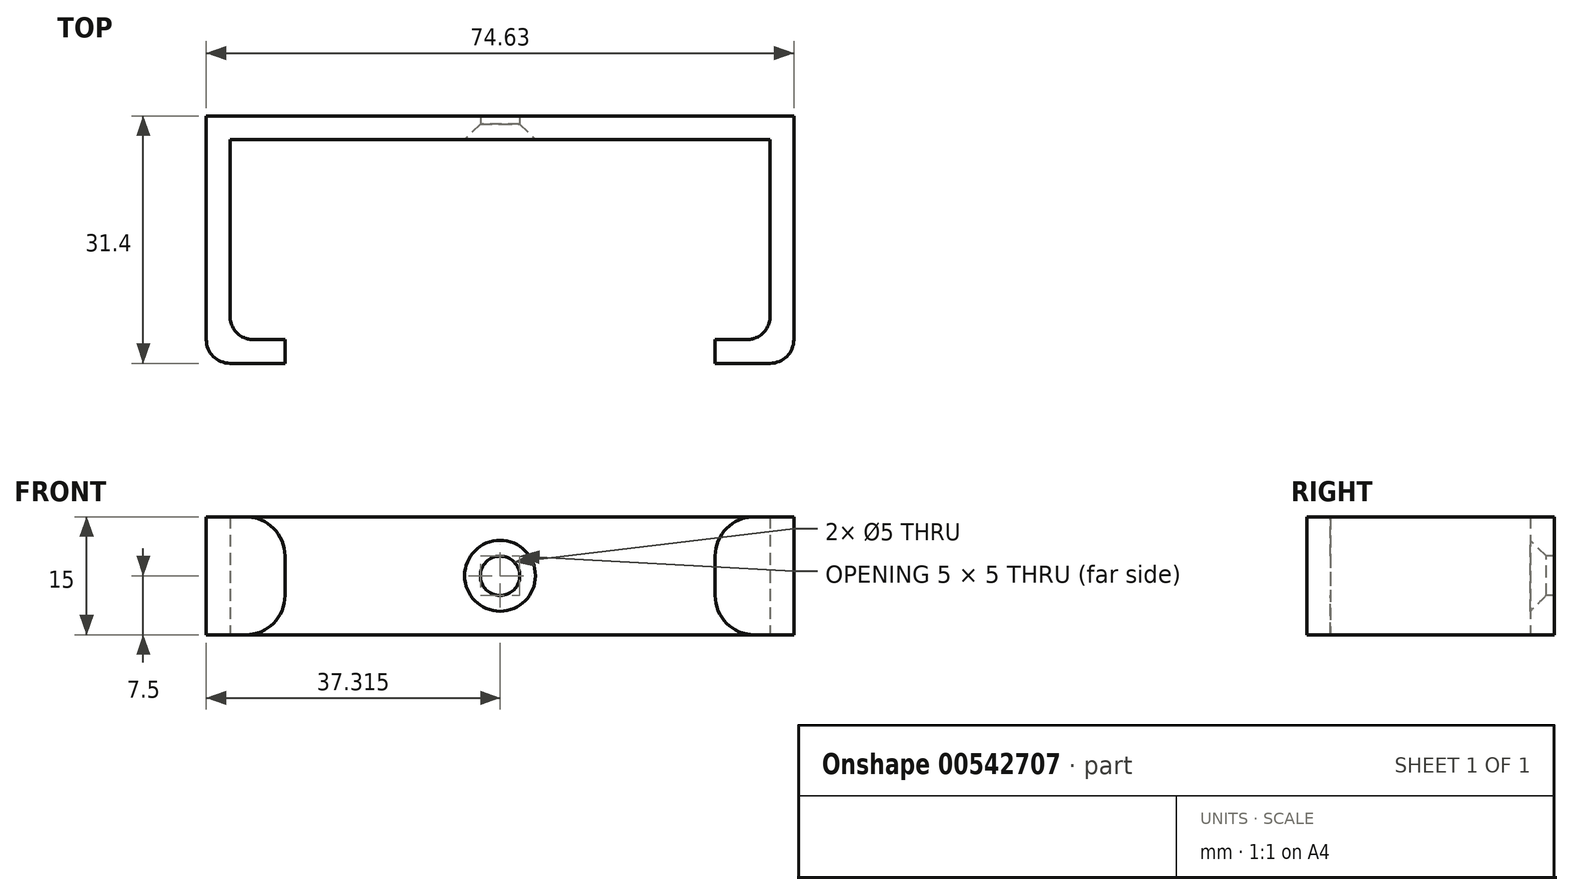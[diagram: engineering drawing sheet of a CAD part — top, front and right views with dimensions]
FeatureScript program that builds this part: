
annotation { "Feature Type Name" : "Feature", "Feature Type Description" : "" }
export const myFeature = defineFeature(function(context is Context, id is Id, definition is map)
    precondition{}
    {
        {
            var Q0;
            Q0=qCreatedBy(makeId("Top.planeOp"),FACE);
            var sketch = newSketch(context, id + "F0", { "sketchPlane" : qUnion([Q0])});
            skLineSegment(sketch, "E0.bottom", {"start": v(0, 0) * mm, "end": v(68.63, 0) * mm});
            skLineSegment(sketch, "E0.top", {"start": v(0, -25.4) * mm, "end": v(68.63, -25.4) * mm});
            skLineSegment(sketch, "E0.left", {"start": v(0, 0) * mm, "end": v(0, -25.4) * mm});
            skLineSegment(sketch, "E0.right", {"start": v(68.63, 0) * mm, "end": v(68.63, -25.4) * mm});
            skLineSegment(sketch, "E1.bottom", {"start": v(-3, 3) * mm, "end": v(71.63, 3) * mm});
            skLineSegment(sketch, "E1.top", {"start": v(-3, -28.4) * mm, "end": v(71.63, -28.4) * mm});
            skLineSegment(sketch, "E1.left", {"start": v(-3, 3) * mm, "end": v(-3, -28.4) * mm});
            skLineSegment(sketch, "E1.right", {"start": v(71.63, 3) * mm, "end": v(71.63, -28.4) * mm});
            skLineSegment(sketch, "E2", {"start": v(61.63, -25.4) * mm, "end": v(61.63, -28.4) * mm});
            skLineSegment(sketch, "E3", {"start": v(7, -25.4) * mm, "end": v(7, -28.4) * mm});
            skSolve(sketch);
        }
        {
            var Q0;
            Q0=makeQuery(id+"F0.imprint","IMPRINT",FACE,{"disambiguationData":[TD([[makeQuery(id+"F0.imprint","IMPRINT",EDGE,{"derivedFrom":sQuery(id+"F0.wireOp",EDGE,"E0.bottom")}),1.0]])]});
            extrude(context, id + "F1", {"entities" : qUnion([Q0]), "depth" : 15 * mm, "offsetDistance" : 25 * mm});
        }
        {
            var Q0;
            Q0=makeQuery(id+"F1.opExtrude","SWEPT_FACE",FACE,{"disambiguationData":[OSD([sQuery(id+"F0.wireOp",EDGE,"E0.bottom")])]});
            var sketch = newSketch(context, id + "F2", { "sketchPlane" : qUnion([Q0])});
            skPoint(sketch, "E4", {"position": v(34.31, 7.5) * mm});
            skPoint(sketch, "E4.positionSnap0", {"position": v(34.31, 15) * mm});
            skSolve(sketch);
        }
        {
            var Q0;
            Q0=sQuery(id+"F2.wireOp",VERTEX,"E4");
            var Q1;
            Q1=makeQuery(id+"F1.opExtrude","SWEPT_BODY",BODY,{"disambiguationData":[OSD([sQuery(id+"F0.wireOp",EDGE,"E0.bottom"),sQuery(id+"F0.wireOp",EDGE,"E0.top"),sQuery(id+"F0.wireOp",EDGE,"E0.left"),sQuery(id+"F0.wireOp",EDGE,"E0.right"),sQuery(id+"F0.wireOp",EDGE,"E1.bottom"),sQuery(id+"F0.wireOp",EDGE,"E1.top"),sQuery(id+"F0.wireOp",EDGE,"E1.left"),sQuery(id+"F0.wireOp",EDGE,"E1.right"),sQuery(id+"F0.wireOp",EDGE,"E2"),sQuery(id+"F0.wireOp",EDGE,"E3")])]});
            hole(context, id + "F3", {"style" : HoleStyle.C_SINK, "endStyle" : HoleEndStyle.BLIND, "holeDiameter" : 5 * mm, "cSinkDiameter" : 9 * mm, "cSinkAngle" : 90 * degree, "holeDepth" : 11 * mm, "isTappedThrough" : true, "tappedDepth" : 100 * mm, "tapClearance" : 3, "startFromSketch" : true, "locations" : qUnion([Q0]), "scope" : qUnion([Q1])});
        }
        {
            var Q0;
            Q0=makeQuery(id+"F1.opExtrude","CAP_EDGE",EDGE,{"disambiguationData":[OSD([sQuery(id+"F0.wireOp",EDGE,"E3")])],"isStart":false});
            var Q1;
            Q1=makeQuery(id+"F1.opExtrude","CAP_EDGE",EDGE,{"disambiguationData":[OSD([sQuery(id+"F0.wireOp",EDGE,"E2")])],"isStart":false});
            var Q2;
            Q2=makeQuery(id+"F1.opExtrude","CAP_EDGE",EDGE,{"disambiguationData":[OSD([sQuery(id+"F0.wireOp",EDGE,"E3")])],"isStart":true});
            var Q3;
            Q3=makeQuery(id+"F1.opExtrude","CAP_EDGE",EDGE,{"disambiguationData":[OSD([sQuery(id+"F0.wireOp",EDGE,"E2")])],"isStart":true});
            fillet(context, id + "F4", {"entities" : qUnion([Q0, Q1, Q2, Q3]), "radius" : 5 * mm, "tangentPropagation" : true, "allowEdgeOverflow" : false});
        }
        {
            var Q0;
            Q0=makeQuery(id+"F1.opExtrude","SWEPT_EDGE",EDGE,{"disambiguationData":[OSD([sQuery(id+"F0.wireOp",EDGE,"E0.top"),sQuery(id+"F0.wireOp",EDGE,"E0.left")])]});
            var Q1;
            Q1=makeQuery(id+"F1.opExtrude","SWEPT_EDGE",EDGE,{"disambiguationData":[OSD([sQuery(id+"F0.wireOp",EDGE,"E1.top"),sQuery(id+"F0.wireOp",EDGE,"E1.left")])]});
            var Q2;
            Q2=makeQuery(id+"F1.opExtrude","SWEPT_EDGE",EDGE,{"disambiguationData":[OSD([sQuery(id+"F0.wireOp",EDGE,"E1.top"),sQuery(id+"F0.wireOp",EDGE,"E1.right")])]});
            var Q3;
            Q3=makeQuery(id+"F1.opExtrude","SWEPT_EDGE",EDGE,{"disambiguationData":[OSD([sQuery(id+"F0.wireOp",EDGE,"E0.top"),sQuery(id+"F0.wireOp",EDGE,"E0.right")])]});
            fillet(context, id + "F5", {"entities" : qUnion([Q0, Q1, Q2, Q3]), "radius" : 3 * mm, "tangentPropagation" : true, "allowEdgeOverflow" : false});
        }
    });
